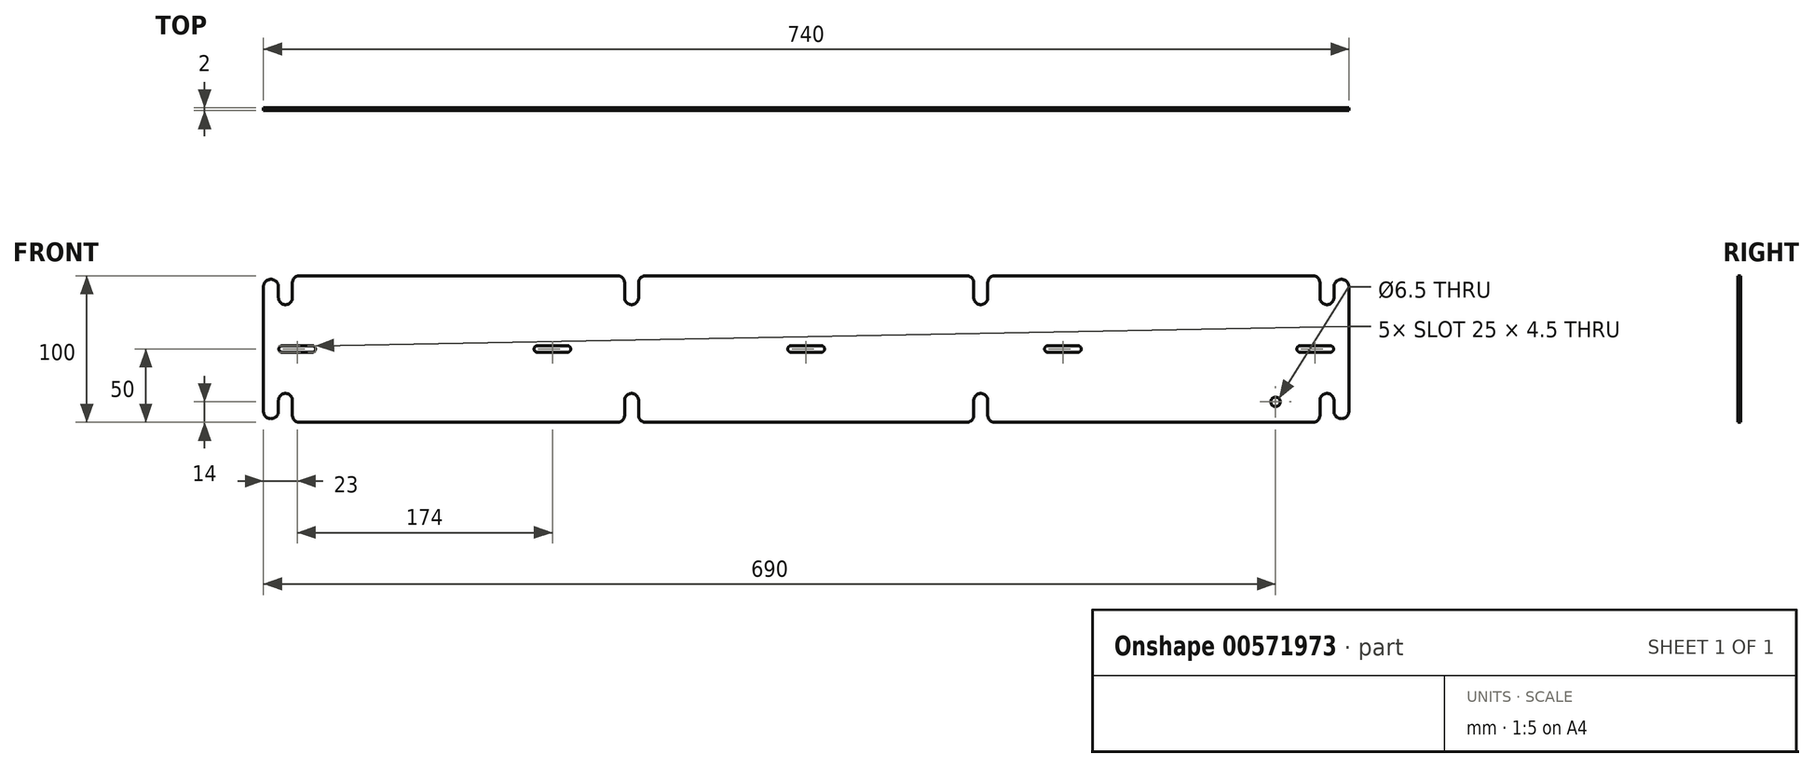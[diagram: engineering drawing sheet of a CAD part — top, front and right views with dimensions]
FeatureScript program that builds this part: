
annotation { "Feature Type Name" : "Feature", "Feature Type Description" : "" }
export const myFeature = defineFeature(function(context is Context, id is Id, definition is map)
    precondition{}
    {
        {
            var Q0;
            Q0=qCreatedBy(makeId("Front.planeOp"),FACE);
            var sketch = newSketch(context, id + "F0", { "sketchPlane" : qUnion([Q0])});
            skLineSegment(sketch, "E0.left", {"start": v(-370, -42.5) * mm, "end": v(-370, 42.5) * mm});
            skLineSegment(sketch, "E0.right", {"start": v(370, -50) * mm, "end": v(370, 50) * mm});
            skPoint(sketch, "E0.middle", {"position": v(0, 0) * mm});
            skArc(sketch, "E1", {"start": v(-359.75, 35) * mm, "mid": v(-355, 30.25) * mm, "end": v(-350.25, 35) * mm});
            skArc(sketch, "E2", {"start": v(-123.75, 35) * mm, "mid": v(-119, 30.25) * mm, "end": v(-114.25, 35) * mm});
            skArc(sketch, "E3", {"start": v(114.25, 35) * mm, "mid": v(119, 30.25) * mm, "end": v(123.75, 35) * mm});
            skArc(sketch, "E4", {"start": v(350.25, 35) * mm, "mid": v(355, 30.25) * mm, "end": v(359.75, 35) * mm});
            skLineSegment(sketch, "E5", {"start": v(-359.75, 35) * mm, "end": v(-359.75, 42.5) * mm});
            skLineSegment(sketch, "E6", {"start": v(-350.25, 35) * mm, "end": v(-350.25, 45) * mm});
            skLineSegment(sketch, "E7", {"start": v(-123.75, 35) * mm, "end": v(-123.75, 45) * mm});
            skLineSegment(sketch, "E8", {"start": v(-114.25, 35) * mm, "end": v(-114.25, 45) * mm});
            skLineSegment(sketch, "E9", {"start": v(114.25, 35) * mm, "end": v(114.25, 45) * mm});
            skLineSegment(sketch, "E10", {"start": v(123.75, 35) * mm, "end": v(123.75, 45) * mm});
            skLineSegment(sketch, "E11", {"start": v(350.25, 35) * mm, "end": v(350.25, 45) * mm});
            skLineSegment(sketch, "E12", {"start": v(359.75, 35) * mm, "end": v(359.75, 42.5) * mm});
            skLineSegment(sketch, "E13.trimOffspring", {"start": v(123.75, 50) * mm, "end": v(350.25, 50) * mm});
            skLineSegment(sketch, "E14.trimOffspring", {"start": v(-109.25, 50) * mm, "end": v(109.25, 50) * mm});
            skLineSegment(sketch, "E15.trimOffspring", {"start": v(-345.25, 50) * mm, "end": v(-128.75, 50) * mm});
            skLineSegment(sketch, "E16.MirrorCS", {"start": v(-345.25, -50) * mm, "end": v(-123.75, -50) * mm});
            skLineSegment(sketch, "E17.MirrorCS", {"start": v(-350.25, -35) * mm, "end": v(-350.25, -45) * mm});
            skArc(sketch, "E18.MirrorCS", {"start": v(-359.75, -35) * mm, "mid": v(-355, -30.25) * mm, "end": v(-350.25, -35) * mm});
            skLineSegment(sketch, "E19.MirrorCS", {"start": v(-359.75, -35) * mm, "end": v(-359.75, -42.5) * mm});
            skLineSegment(sketch, "E20.MirrorCS", {"start": v(-114.25, -50) * mm, "end": v(114.25, -50) * mm});
            skLineSegment(sketch, "E21.MirrorCS", {"start": v(-114.25, -35) * mm, "end": v(-114.25, -45) * mm});
            skLineSegment(sketch, "E22.MirrorCS", {"start": v(-123.75, -35) * mm, "end": v(-123.75, -45) * mm});
            skArc(sketch, "E23.MirrorCS", {"start": v(-123.75, -35) * mm, "mid": v(-119, -30.25) * mm, "end": v(-114.25, -35) * mm});
            skLineSegment(sketch, "E24.MirrorCS", {"start": v(-345.25, -50) * mm, "end": v(-128.75, -50) * mm});
            skArc(sketch, "E25.MirrorCS", {"start": v(114.25, -35) * mm, "mid": v(119, -30.25) * mm, "end": v(123.75, -35) * mm});
            skLineSegment(sketch, "E26.MirrorCS", {"start": v(123.75, -50) * mm, "end": v(350.25, -50) * mm});
            skLineSegment(sketch, "E27.MirrorCS", {"start": v(114.25, -35) * mm, "end": v(114.25, -45) * mm});
            skLineSegment(sketch, "E28.MirrorCS", {"start": v(123.75, -35) * mm, "end": v(123.75, -45) * mm});
            skLineSegment(sketch, "E29.MirrorCS", {"start": v(350.25, -35) * mm, "end": v(350.25, -45) * mm});
            skLineSegment(sketch, "E30.MirrorCS", {"start": v(359.75, -35) * mm, "end": v(359.75, -42.5) * mm});
            skArc(sketch, "E31.MirrorCS", {"start": v(350.25, -35) * mm, "mid": v(355, -30.25) * mm, "end": v(359.75, -35) * mm});
            skLineSegment(sketch, "E32.MirrorCS", {"start": v(128.75, -50) * mm, "end": v(350.25, -50) * mm});
            skLineSegment(sketch, "E33.MirrorCS", {"start": v(370, 50) * mm, "end": v(370, -50) * mm});
            skLineSegment(sketch, "E34.trimOffspring", {"start": v(123.75, -50) * mm, "end": v(345.25, -50) * mm});
            skLineSegment(sketch, "E35.trimOffspring", {"start": v(-109.25, -50) * mm, "end": v(109.25, -50) * mm});
            skLineSegment(sketch, "E36.trimOffspring", {"start": v(-350.25, -50) * mm, "end": v(-123.75, -50) * mm});
            skArc(sketch, "E37", {"start": v(-359.75, 42.5) * mm, "mid": v(-364.87, 47.5) * mm, "end": v(-370, 42.5) * mm});
            skPoint(sketch, "E37.endSnap0", {"position": v(-359.75, 42.5) * mm});
            skPoint(sketch, "E0.top.end.orphan", {"position": v(-359.75, 50) * mm});
            skPoint(sketch, "E38.orphan", {"position": v(-370, 50) * mm});
            skPoint(sketch, "E39.visualSharp", {"position": v(-350.25, 50) * mm});
            skArc(sketch, "E39.filletArc", {"start": v(-345.25, 50) * mm, "mid": v(-348.79, 48.54) * mm, "end": v(-350.25, 45) * mm});
            skArc(sketch, "E40.MirrorCS", {"start": v(-359.75, -42.5) * mm, "mid": v(-364.87, -47.5) * mm, "end": v(-370, -42.5) * mm});
            skArc(sketch, "E41.MirrorCS", {"start": v(-345.25, -50) * mm, "mid": v(-348.79, -48.54) * mm, "end": v(-350.25, -45) * mm});
            skPoint(sketch, "E42.MirrorP", {"position": v(-370, -50) * mm});
            skPoint(sketch, "E43.MirrorP", {"position": v(-359.75, -42.5) * mm});
            skPoint(sketch, "E44.MirrorP", {"position": v(-350.25, -50) * mm});
            skLineSegment(sketch, "E45.MirrorCS", {"start": v(-370, 50) * mm, "end": v(-370, -42.5) * mm});
            skPoint(sketch, "E0.bottom.end.orphan", {"position": v(-359.75, -50) * mm});
            skLineSegment(sketch, "E46.MirrorCS", {"start": v(345.25, -50) * mm, "end": v(123.75, -50) * mm});
            skArc(sketch, "E47.MirrorCS", {"start": v(345.25, -50) * mm, "mid": v(348.79, -48.54) * mm, "end": v(350.25, -45) * mm});
            skPoint(sketch, "E48.MirrorP", {"position": v(370, -50) * mm});
            skPoint(sketch, "E49.MirrorP", {"position": v(350.25, -50) * mm});
            skArc(sketch, "E50.MirrorCS", {"start": v(359.75, -35) * mm, "mid": v(355, -30.25) * mm, "end": v(350.25, -35) * mm});
            skPoint(sketch, "E51.MirrorP", {"position": v(359.75, -50) * mm});
            skLineSegment(sketch, "E52.MirrorCS", {"start": v(370, -42.5) * mm, "end": v(370, 42.5) * mm});
            skArc(sketch, "E53.MirrorCS", {"start": v(359.75, -42.5) * mm, "mid": v(364.87, -47.5) * mm, "end": v(370, -42.5) * mm});
            skLineSegment(sketch, "E54.MirrorCS", {"start": v(370, 50) * mm, "end": v(370, -42.5) * mm});
            skPoint(sketch, "E55.MirrorP", {"position": v(359.75, -42.5) * mm});
            skArc(sketch, "E56.MirrorCS", {"start": v(345.25, 50) * mm, "mid": v(348.79, 48.54) * mm, "end": v(350.25, 45) * mm});
            skPoint(sketch, "E57.MirrorP", {"position": v(370, 50) * mm});
            skLineSegment(sketch, "E58.MirrorCS", {"start": v(345.25, 50) * mm, "end": v(128.75, 50) * mm});
            skPoint(sketch, "E59.MirrorP", {"position": v(359.75, 50) * mm});
            skArc(sketch, "E60.MirrorCS", {"start": v(359.75, 35) * mm, "mid": v(355, 30.25) * mm, "end": v(350.25, 35) * mm});
            skPoint(sketch, "E61.MirrorP", {"position": v(350.25, 50) * mm});
            skArc(sketch, "E62.MirrorCS", {"start": v(359.75, 42.5) * mm, "mid": v(364.87, 47.5) * mm, "end": v(370, 42.5) * mm});
            skPoint(sketch, "E63.MirrorP", {"position": v(359.75, 42.5) * mm});
            skPoint(sketch, "E64.visualSharp", {"position": v(-123.75, 50) * mm});
            skArc(sketch, "E64.filletArc", {"start": v(-123.75, 45) * mm, "mid": v(-125.21, 48.54) * mm, "end": v(-128.75, 50) * mm});
            skPoint(sketch, "E65.visualSharp", {"position": v(-114.25, 50) * mm});
            skArc(sketch, "E65.filletArc", {"start": v(-109.25, 50) * mm, "mid": v(-112.79, 48.54) * mm, "end": v(-114.25, 45) * mm});
            skPoint(sketch, "E66.visualSharp", {"position": v(-123.75, -50) * mm});
            skArc(sketch, "E66.filletArc", {"start": v(-128.75, -50) * mm, "mid": v(-125.21, -48.54) * mm, "end": v(-123.75, -45) * mm});
            skPoint(sketch, "E67.visualSharp", {"position": v(-114.25, -50) * mm});
            skArc(sketch, "E67.filletArc", {"start": v(-114.25, -45) * mm, "mid": v(-112.79, -48.54) * mm, "end": v(-109.25, -50) * mm});
            skPoint(sketch, "E68.visualSharp", {"position": v(114.25, 50) * mm});
            skArc(sketch, "E68.filletArc", {"start": v(114.25, 45) * mm, "mid": v(112.79, 48.54) * mm, "end": v(109.25, 50) * mm});
            skPoint(sketch, "E69.visualSharp", {"position": v(123.75, 50) * mm});
            skArc(sketch, "E69.filletArc", {"start": v(128.75, 50) * mm, "mid": v(125.21, 48.54) * mm, "end": v(123.75, 45) * mm});
            skPoint(sketch, "E70.visualSharp", {"position": v(114.25, -50) * mm});
            skArc(sketch, "E70.filletArc", {"start": v(109.25, -50) * mm, "mid": v(112.79, -48.54) * mm, "end": v(114.25, -45) * mm});
            skPoint(sketch, "E71.visualSharp", {"position": v(123.75, -50) * mm});
            skArc(sketch, "E71.filletArc", {"start": v(123.75, -45) * mm, "mid": v(125.21, -48.54) * mm, "end": v(128.75, -50) * mm});
            skSolve(sketch);
        }
        {
            var Q0;
            Q0 = qSketchRegion(id + "F0", true);
            extrude(context, id + "F1", {"entities" : qUnion([Q0]), "endBound" : BoundingType.SYMMETRIC, "depth" : 2 * mm, "offsetDistance" : 25 * mm});
        }
        {
            var Q0;
            Q0=makeQuery(id+"F1.opExtrude","CAP_FACE",FACE,{"disambiguationData":[OSD([sQuery(id+"F0.wireOp",EDGE,"E1"),sQuery(id+"F0.wireOp",EDGE,"E2"),sQuery(id+"F0.wireOp",EDGE,"E3"),sQuery(id+"F0.wireOp",EDGE,"E5"),sQuery(id+"F0.wireOp",EDGE,"E6"),sQuery(id+"F0.wireOp",EDGE,"E7"),sQuery(id+"F0.wireOp",EDGE,"E8"),sQuery(id+"F0.wireOp",EDGE,"E9"),sQuery(id+"F0.wireOp",EDGE,"E10"),sQuery(id+"F0.wireOp",EDGE,"E14.trimOffspring"),sQuery(id+"F0.wireOp",EDGE,"E15.trimOffspring"),sQuery(id+"F0.wireOp",EDGE,"E21.MirrorCS"),sQuery(id+"F0.wireOp",EDGE,"E22.MirrorCS"),sQuery(id+"F0.wireOp",EDGE,"E23.MirrorCS"),sQuery(id+"F0.wireOp",EDGE,"E25.MirrorCS"),sQuery(id+"F0.wireOp",EDGE,"E27.MirrorCS"),sQuery(id+"F0.wireOp",EDGE,"E28.MirrorCS"),sQuery(id+"F0.wireOp",EDGE,"E35.trimOffspring"),sQuery(id+"F0.wireOp",EDGE,"E37"),sQuery(id+"F0.wireOp",EDGE,"E39.filletArc"),sQuery(id+"F0.wireOp",EDGE,"E40.MirrorCS"),sQuery(id+"F0.wireOp",EDGE,"E17.MirrorCS"),sQuery(id+"F0.wireOp",EDGE,"E19.MirrorCS"),sQuery(id+"F0.wireOp",EDGE,"E41.MirrorCS"),sQuery(id+"F0.wireOp",EDGE,"E18.MirrorCS"),sQuery(id+"F0.wireOp",EDGE,"E16.MirrorCS"),sQuery(id+"F0.wireOp",EDGE,"E45.MirrorCS"),sQuery(id+"F0.wireOp",EDGE,"E47.MirrorCS"),sQuery(id+"F0.wireOp",EDGE,"E46.MirrorCS"),sQuery(id+"F0.wireOp",EDGE,"E50.MirrorCS"),sQuery(id+"F0.wireOp",EDGE,"E29.MirrorCS"),sQuery(id+"F0.wireOp",EDGE,"E30.MirrorCS"),sQuery(id+"F0.wireOp",EDGE,"E53.MirrorCS"),sQuery(id+"F0.wireOp",EDGE,"E56.MirrorCS"),sQuery(id+"F0.wireOp",EDGE,"E11"),sQuery(id+"F0.wireOp",EDGE,"E12"),sQuery(id+"F0.wireOp",EDGE,"E58.MirrorCS"),sQuery(id+"F0.wireOp",EDGE,"E60.MirrorCS"),sQuery(id+"F0.wireOp",EDGE,"E54.MirrorCS"),sQuery(id+"F0.wireOp",EDGE,"E62.MirrorCS"),sQuery(id+"F0.wireOp",EDGE,"E64.filletArc"),sQuery(id+"F0.wireOp",EDGE,"E65.filletArc"),sQuery(id+"F0.wireOp",EDGE,"E66.filletArc"),sQuery(id+"F0.wireOp",EDGE,"E67.filletArc"),sQuery(id+"F0.wireOp",EDGE,"E68.filletArc"),sQuery(id+"F0.wireOp",EDGE,"E69.filletArc"),sQuery(id+"F0.wireOp",EDGE,"E70.filletArc"),sQuery(id+"F0.wireOp",EDGE,"E71.filletArc")])],"isStart":false});
            var sketch = newSketch(context, id + "F2", { "sketchPlane" : qUnion([Q0])});
            skLineSegment(sketch, "E72.bottom", {"start": v(-336.75, -2.25) * mm, "end": v(-357.25, -2.25) * mm});
            skLineSegment(sketch, "E72.top", {"start": v(-336.75, 2.25) * mm, "end": v(-357.25, 2.25) * mm});
            skPoint(sketch, "E72.middle", {"position": v(-347, 0) * mm});
            skArc(sketch, "E73", {"start": v(-357.25, 2.25) * mm, "mid": v(-359.5, 0) * mm, "end": v(-357.25, -2.25) * mm});
            skArc(sketch, "E74", {"start": v(-336.75, -2.25) * mm, "mid": v(-334.5, 0) * mm, "end": v(-336.75, 2.25) * mm});
            skLineSegment(sketch, "E75.bottom", {"start": v(-162.75, -2.25) * mm, "end": v(-183.25, -2.25) * mm});
            skLineSegment(sketch, "E75.top", {"start": v(-162.75, 2.25) * mm, "end": v(-183.25, 2.25) * mm});
            skPoint(sketch, "E75.middle", {"position": v(-173, 0) * mm});
            skArc(sketch, "E76", {"start": v(-183.25, 2.25) * mm, "mid": v(-185.5, 0) * mm, "end": v(-183.25, -2.25) * mm});
            skArc(sketch, "E77", {"start": v(-162.75, -2.25) * mm, "mid": v(-160.5, 0) * mm, "end": v(-162.75, 2.25) * mm});
            skLineSegment(sketch, "E78.bottom", {"start": v(10.25, -2.25) * mm, "end": v(-10.25, -2.25) * mm});
            skLineSegment(sketch, "E78.top", {"start": v(10.25, 2.25) * mm, "end": v(-10.25, 2.25) * mm});
            skPoint(sketch, "E78.middle", {"position": v(0, 0) * mm});
            skArc(sketch, "E79", {"start": v(-10.25, 2.25) * mm, "mid": v(-12.5, 0) * mm, "end": v(-10.25, -2.25) * mm});
            skArc(sketch, "E80", {"start": v(10.25, -2.25) * mm, "mid": v(12.5, 0) * mm, "end": v(10.25, 2.25) * mm});
            skLineSegment(sketch, "E81.bottom", {"start": v(185.25, -2.25) * mm, "end": v(164.75, -2.25) * mm});
            skLineSegment(sketch, "E81.top", {"start": v(185.25, 2.25) * mm, "end": v(164.75, 2.25) * mm});
            skPoint(sketch, "E81.middle", {"position": v(175, 0) * mm});
            skArc(sketch, "E82", {"start": v(164.75, 2.25) * mm, "mid": v(162.5, 0) * mm, "end": v(164.75, -2.25) * mm});
            skArc(sketch, "E83", {"start": v(185.25, -2.25) * mm, "mid": v(187.5, 0) * mm, "end": v(185.25, 2.25) * mm});
            skLineSegment(sketch, "E84.bottom", {"start": v(357.25, -2.25) * mm, "end": v(336.75, -2.25) * mm});
            skLineSegment(sketch, "E84.top", {"start": v(357.25, 2.25) * mm, "end": v(336.75, 2.25) * mm});
            skPoint(sketch, "E84.middle", {"position": v(347, 0) * mm});
            skArc(sketch, "E85", {"start": v(336.75, 2.25) * mm, "mid": v(334.5, 0) * mm, "end": v(336.75, -2.25) * mm});
            skArc(sketch, "E86", {"start": v(357.25, -2.25) * mm, "mid": v(359.5, 0) * mm, "end": v(357.25, 2.25) * mm});
            skSolve(sketch);
        }
        {
            var Q0;
            Q0 = qSketchRegion(id + "F2", true);
            extrude(context, id + "F3", {"entities" : qUnion([Q0]), "operationType" : NewBodyOperationType.REMOVE, "oppositeDirection" : true, "depth" : 25 * mm, "offsetDistance" : 25 * mm});
        }
        {
            var Q0;
            Q0=makeQuery(id+"F1.opExtrude","CAP_FACE",FACE,{"disambiguationData":[OSD([sQuery(id+"F0.wireOp",EDGE,"E1"),sQuery(id+"F0.wireOp",EDGE,"E2"),sQuery(id+"F0.wireOp",EDGE,"E3"),sQuery(id+"F0.wireOp",EDGE,"E5"),sQuery(id+"F0.wireOp",EDGE,"E6"),sQuery(id+"F0.wireOp",EDGE,"E7"),sQuery(id+"F0.wireOp",EDGE,"E8"),sQuery(id+"F0.wireOp",EDGE,"E9"),sQuery(id+"F0.wireOp",EDGE,"E10"),sQuery(id+"F0.wireOp",EDGE,"E14.trimOffspring"),sQuery(id+"F0.wireOp",EDGE,"E15.trimOffspring"),sQuery(id+"F0.wireOp",EDGE,"E21.MirrorCS"),sQuery(id+"F0.wireOp",EDGE,"E22.MirrorCS"),sQuery(id+"F0.wireOp",EDGE,"E23.MirrorCS"),sQuery(id+"F0.wireOp",EDGE,"E25.MirrorCS"),sQuery(id+"F0.wireOp",EDGE,"E27.MirrorCS"),sQuery(id+"F0.wireOp",EDGE,"E28.MirrorCS"),sQuery(id+"F0.wireOp",EDGE,"E35.trimOffspring"),sQuery(id+"F0.wireOp",EDGE,"E37"),sQuery(id+"F0.wireOp",EDGE,"E39.filletArc"),sQuery(id+"F0.wireOp",EDGE,"E40.MirrorCS"),sQuery(id+"F0.wireOp",EDGE,"E17.MirrorCS"),sQuery(id+"F0.wireOp",EDGE,"E19.MirrorCS"),sQuery(id+"F0.wireOp",EDGE,"E41.MirrorCS"),sQuery(id+"F0.wireOp",EDGE,"E18.MirrorCS"),sQuery(id+"F0.wireOp",EDGE,"E16.MirrorCS"),sQuery(id+"F0.wireOp",EDGE,"E45.MirrorCS"),sQuery(id+"F0.wireOp",EDGE,"E47.MirrorCS"),sQuery(id+"F0.wireOp",EDGE,"E46.MirrorCS"),sQuery(id+"F0.wireOp",EDGE,"E50.MirrorCS"),sQuery(id+"F0.wireOp",EDGE,"E29.MirrorCS"),sQuery(id+"F0.wireOp",EDGE,"E30.MirrorCS"),sQuery(id+"F0.wireOp",EDGE,"E53.MirrorCS"),sQuery(id+"F0.wireOp",EDGE,"E56.MirrorCS"),sQuery(id+"F0.wireOp",EDGE,"E11"),sQuery(id+"F0.wireOp",EDGE,"E12"),sQuery(id+"F0.wireOp",EDGE,"E58.MirrorCS"),sQuery(id+"F0.wireOp",EDGE,"E60.MirrorCS"),sQuery(id+"F0.wireOp",EDGE,"E54.MirrorCS"),sQuery(id+"F0.wireOp",EDGE,"E62.MirrorCS"),sQuery(id+"F0.wireOp",EDGE,"E64.filletArc"),sQuery(id+"F0.wireOp",EDGE,"E65.filletArc"),sQuery(id+"F0.wireOp",EDGE,"E66.filletArc"),sQuery(id+"F0.wireOp",EDGE,"E67.filletArc"),sQuery(id+"F0.wireOp",EDGE,"E68.filletArc"),sQuery(id+"F0.wireOp",EDGE,"E69.filletArc"),sQuery(id+"F0.wireOp",EDGE,"E70.filletArc"),sQuery(id+"F0.wireOp",EDGE,"E71.filletArc")])],"isStart":false});
            var sketch = newSketch(context, id + "F4", { "sketchPlane" : qUnion([Q0])});
            skCircle(sketch, "E87", {"center": v(320, -36) * mm, "radius": 3.25 * mm});
            skSolve(sketch);
        }
        {
            var Q0;
            Q0 = qSketchRegion(id + "F4", true);
            extrude(context, id + "F5", {"entities" : qUnion([Q0]), "operationType" : NewBodyOperationType.REMOVE, "oppositeDirection" : true, "depth" : 25 * mm, "offsetDistance" : 25 * mm});
        }
    });
